# Revit family: Accessories_Set-Grohe-Essentials_Master-40823_Series
name_source: partatom
category: Specialty Equipment
revit_build: Autodesk Revit 2014 (Build: 20130308_1515(x64)
units: mm (PartAtom-declared; Revit-internal decimal feet)

## types (2) — shared parameters
Assembly Code = C1030200
Description = Essentials Master bathroom accessories set 4-in-1
Height = 7 7/8"
Installation Type = Wall Mounted
Length = 25 3/4"
Manufacturer = Grohe
Price = Prices may vary. Please consult Manufacturer Representative for most up-to-date price list.
Product Page URL = https://www.grohe.us
Robe Hook 40364 = No
Towel Bar 40366 = No
Towel Ring 40365 = No
URL = https://www.grohe.us

## per-type parameters (varying)
| type | Default Elevation | Finish | Material | Toilet Paper Holder 40689 |
| 40823001 | 16" | Metal-Grohe-001-Chrome | Metal-Grohe-001-Chrome | Yes |
| 40823EN1 | 40" | Metal-Grohe-EN1-Brushed Nickel | Metal-Grohe-EN1-Brushed Nickel | No |

note: column(s) folded — value = type name in every type: Model

## geometry (parser evidence)
native form markers: Sweep x3
no freeform markers — native parametric forms only
